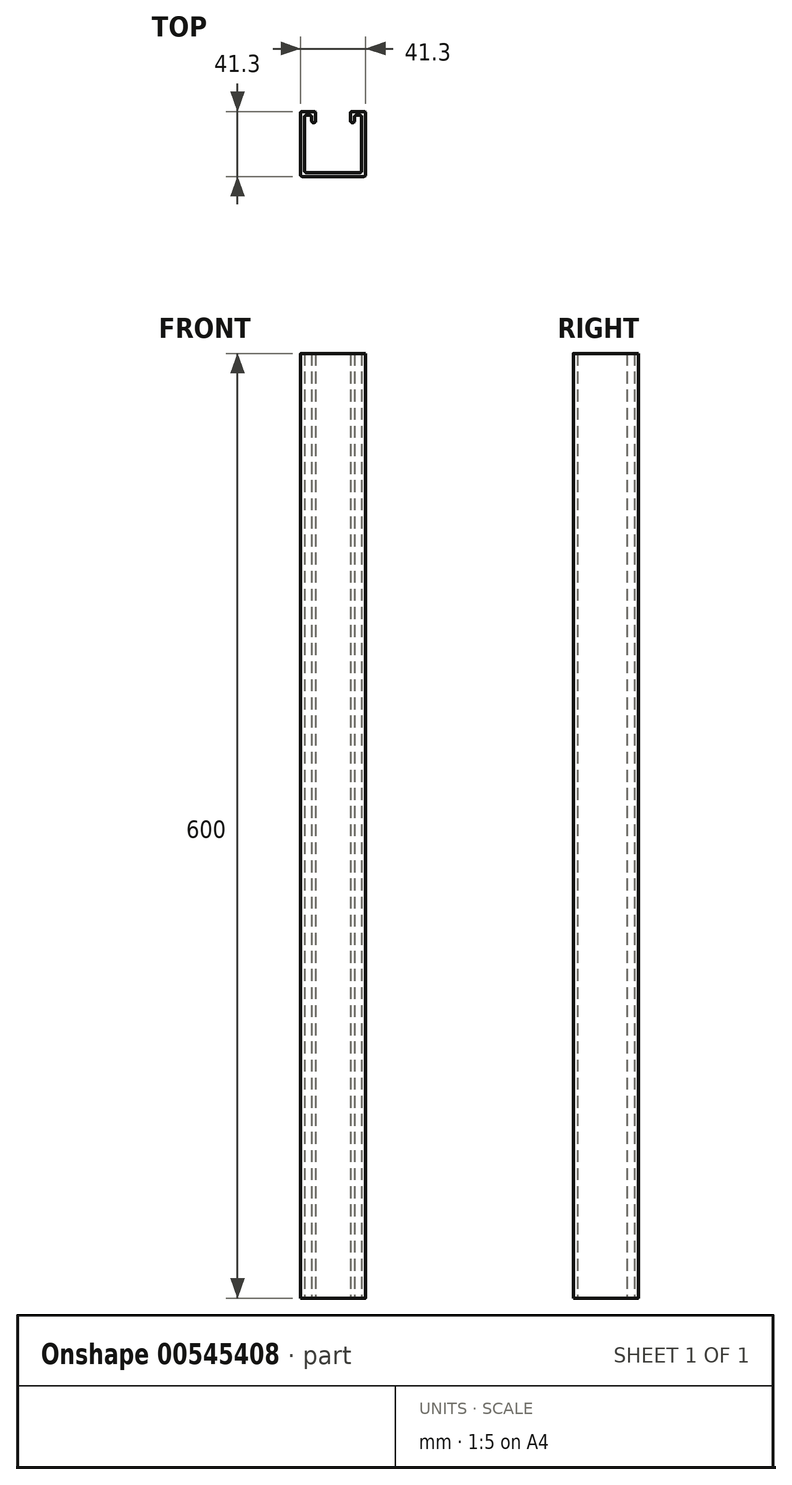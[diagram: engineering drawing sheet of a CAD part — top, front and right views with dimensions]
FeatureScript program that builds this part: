
annotation { "Feature Type Name" : "Feature", "Feature Type Description" : "" }
export const myFeature = defineFeature(function(context is Context, id is Id, definition is map)
    precondition{}
    {
        {
            var Q0;
            Q0=qCreatedBy(makeId("Top.planeOp"),FACE);
            var sketch = newSketch(context, id + "F0", { "sketchPlane" : qUnion([Q0])});
            skLineSegment(sketch, "E0", {"start": v(-11.1, 11.7) * mm, "end": v(-11.1, 18.8) * mm});
            skLineSegment(sketch, "E1", {"start": v(-11.1, 18.8) * mm, "end": v(-20.65, 18.8) * mm});
            skLineSegment(sketch, "E2", {"start": v(-20.65, 18.8) * mm, "end": v(-20.65, -22.5) * mm});
            skLineSegment(sketch, "E3", {"start": v(-20.65, -22.5) * mm, "end": v(20.65, -22.5) * mm});
            skLineSegment(sketch, "E4", {"start": v(20.65, -22.5) * mm, "end": v(20.65, 18.8) * mm});
            skLineSegment(sketch, "E5", {"start": v(20.65, 18.8) * mm, "end": v(11.1, 18.8) * mm});
            skLineSegment(sketch, "E6", {"start": v(11.1, 18.8) * mm, "end": v(11.1, 11.7) * mm});
            skLineSegment(sketch, "E7", {"start": v(-11.1, 11.7) * mm, "end": v(-13.6, 11.7) * mm});
            skLineSegment(sketch, "E8", {"start": v(-13.6, 11.7) * mm, "end": v(-13.6, 16.3) * mm});
            skLineSegment(sketch, "E9", {"start": v(-13.6, 16.3) * mm, "end": v(-18.15, 16.3) * mm});
            skLineSegment(sketch, "E10", {"start": v(-18.15, 16.3) * mm, "end": v(-18.15, -20) * mm});
            skLineSegment(sketch, "E11", {"start": v(-18.15, -20) * mm, "end": v(18.15, -20) * mm});
            skLineSegment(sketch, "E12", {"start": v(18.15, -20) * mm, "end": v(18.15, 16.3) * mm});
            skLineSegment(sketch, "E13", {"start": v(18.15, 16.3) * mm, "end": v(13.6, 16.3) * mm});
            skLineSegment(sketch, "E14", {"start": v(13.6, 16.3) * mm, "end": v(13.6, 11.7) * mm});
            skLineSegment(sketch, "E15", {"start": v(13.6, 11.7) * mm, "end": v(11.1, 11.7) * mm});
            skSolve(sketch);
        }
        {
            var Q0;
            Q0=makeQuery(id+"F0.imprint","IMPRINT",FACE,{"disambiguationData":[TD([[makeQuery(id+"F0.imprint","IMPRINT",EDGE,{"derivedFrom":sQuery(id+"F0.wireOp",EDGE,"E0")}),1.0]])]});
            extrude(context, id + "F1", {"entities" : qUnion([Q0]), "depth" : 600 * mm, "offsetDistance" : 25 * mm});
        }
        {
            var Q0;
            Q0=makeQuery(id+"F1.opExtrude","SWEPT_EDGE",EDGE,{"disambiguationData":[OSD([sQuery(id+"F0.wireOp",EDGE,"E1"),sQuery(id+"F0.wireOp",EDGE,"E2")])]});
            var Q1;
            Q1=makeQuery(id+"F1.opExtrude","SWEPT_EDGE",EDGE,{"disambiguationData":[OSD([sQuery(id+"F0.wireOp",EDGE,"E5"),sQuery(id+"F0.wireOp",EDGE,"E6")])]});
            var Q2;
            Q2=makeQuery(id+"F1.opExtrude","SWEPT_EDGE",EDGE,{"disambiguationData":[OSD([sQuery(id+"F0.wireOp",EDGE,"E4"),sQuery(id+"F0.wireOp",EDGE,"E5")])]});
            var Q3;
            Q3=makeQuery(id+"F1.opExtrude","SWEPT_EDGE",EDGE,{"disambiguationData":[OSD([sQuery(id+"F0.wireOp",EDGE,"E0"),sQuery(id+"F0.wireOp",EDGE,"E1")])]});
            var Q4;
            Q4=makeQuery(id+"F1.opExtrude","SWEPT_EDGE",EDGE,{"disambiguationData":[OSD([sQuery(id+"F0.wireOp",EDGE,"E2"),sQuery(id+"F0.wireOp",EDGE,"E3")])]});
            var Q5;
            Q5=makeQuery(id+"F1.opExtrude","SWEPT_EDGE",EDGE,{"disambiguationData":[OSD([sQuery(id+"F0.wireOp",EDGE,"E11"),sQuery(id+"F0.wireOp",EDGE,"E12")])]});
            var Q6;
            Q6=makeQuery(id+"F1.opExtrude","SWEPT_EDGE",EDGE,{"disambiguationData":[OSD([sQuery(id+"F0.wireOp",EDGE,"E9"),sQuery(id+"F0.wireOp",EDGE,"E10")])]});
            var Q7;
            Q7=makeQuery(id+"F1.opExtrude","SWEPT_EDGE",EDGE,{"disambiguationData":[OSD([sQuery(id+"F0.wireOp",EDGE,"E0"),sQuery(id+"F0.wireOp",EDGE,"E7")])]});
            var Q8;
            Q8=makeQuery(id+"F1.opExtrude","SWEPT_EDGE",EDGE,{"disambiguationData":[OSD([sQuery(id+"F0.wireOp",EDGE,"E8"),sQuery(id+"F0.wireOp",EDGE,"E9")])]});
            var Q9;
            Q9=makeQuery(id+"F1.opExtrude","SWEPT_EDGE",EDGE,{"disambiguationData":[OSD([sQuery(id+"F0.wireOp",EDGE,"E7"),sQuery(id+"F0.wireOp",EDGE,"E8")])]});
            var Q10;
            Q10=makeQuery(id+"F1.opExtrude","SWEPT_EDGE",EDGE,{"disambiguationData":[OSD([sQuery(id+"F0.wireOp",EDGE,"E10"),sQuery(id+"F0.wireOp",EDGE,"E11")])]});
            var Q11;
            Q11=makeQuery(id+"F1.opExtrude","SWEPT_EDGE",EDGE,{"disambiguationData":[OSD([sQuery(id+"F0.wireOp",EDGE,"E3"),sQuery(id+"F0.wireOp",EDGE,"E4")])]});
            var Q12;
            Q12=makeQuery(id+"F1.opExtrude","SWEPT_EDGE",EDGE,{"disambiguationData":[OSD([sQuery(id+"F0.wireOp",EDGE,"E14"),sQuery(id+"F0.wireOp",EDGE,"E15")])]});
            var Q13;
            Q13=makeQuery(id+"F1.opExtrude","SWEPT_EDGE",EDGE,{"disambiguationData":[OSD([sQuery(id+"F0.wireOp",EDGE,"E6"),sQuery(id+"F0.wireOp",EDGE,"E15")])]});
            var Q14;
            Q14=makeQuery(id+"F1.opExtrude","SWEPT_EDGE",EDGE,{"disambiguationData":[OSD([sQuery(id+"F0.wireOp",EDGE,"E13"),sQuery(id+"F0.wireOp",EDGE,"E14")])]});
            var Q15;
            Q15=makeQuery(id+"F1.opExtrude","SWEPT_EDGE",EDGE,{"disambiguationData":[OSD([sQuery(id+"F0.wireOp",EDGE,"E12"),sQuery(id+"F0.wireOp",EDGE,"E13")])]});
            fillet(context, id + "F2", {"entities" : qUnion([Q0, Q1, Q2, Q3, Q4, Q5, Q6, Q7, Q8, Q9, Q10, Q11, Q12, Q13, Q14, Q15]), "radius" : 1 * mm, "tangentPropagation" : true, "allowEdgeOverflow" : false});
        }
    });
